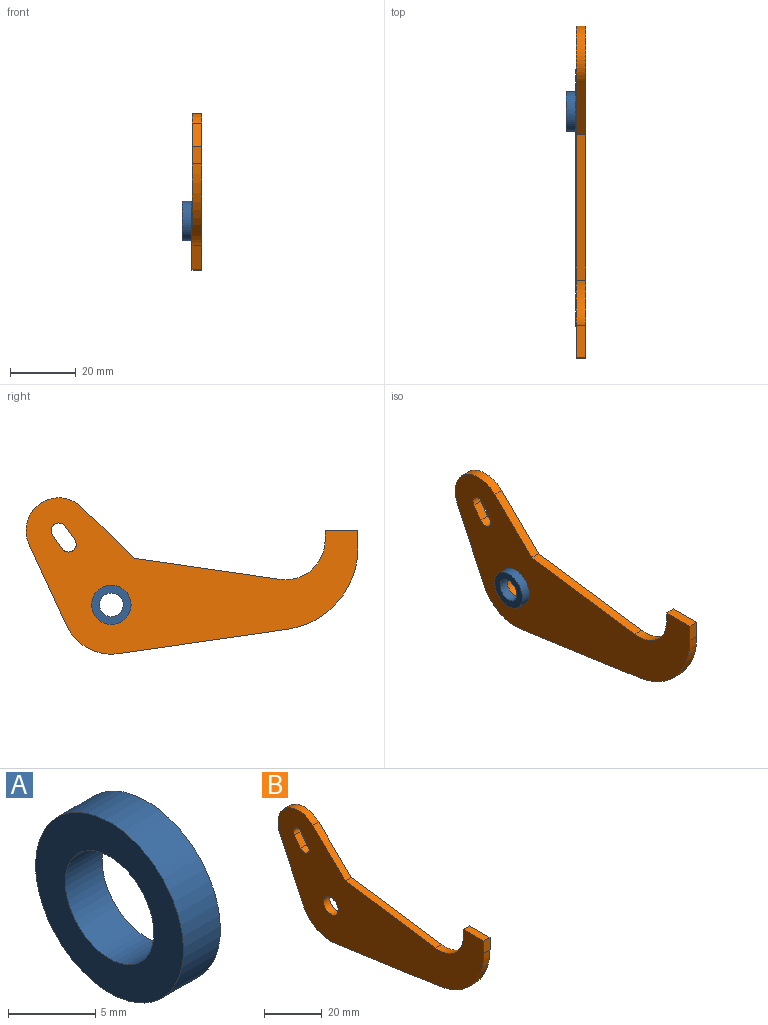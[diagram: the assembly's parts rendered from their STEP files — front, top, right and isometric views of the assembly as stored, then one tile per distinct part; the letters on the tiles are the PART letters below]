
ASSEMBLY  parts=2 mates=1
PART A: 4 faces, bbox 3x12x12 mm
  f0: plane 12x12mm, normal (1,0,0), area 72.4mm2, adj f1,f2
  f1: cylinder r=3.6mm len=7.2mm, axis (-1,0,0), area 67.9mm2, adj f0,f3
  f2: cylinder r=6mm len=12mm, axis (-1,0,0), area 113.1mm2, adj f0,f3
  f3: plane 12x12mm, normal (-1,0,0), area 72.4mm2, adj f1,f2
PART B: 18 faces, bbox 3x101x47.6 mm
  f0: plane 100.95x47.55mm, normal (1,0,0), area 2358.5mm2, adj f1,f2,f3,f4,f5,f6,f7,f8
  f1: cylinder r=2.35mm len=4.27mm, axis (-1,0,0), area 22.1mm2, adj f0,f11,f12,f17
  f2: plane 51.43x7.42mm, normal (0,-0.14,-0.99), area 155.9mm2, adj f0,f3,f10,f17
  f3: cylinder r=15mm len=15.75mm, axis (-1,0,0), area 57.6mm2, adj f0,f2,f4,f17
  f4: plane 24.65x11.41mm, normal (0,0.91,-0.42), area 81.5mm2, adj f0,f3,f5,f17
  f5: cylinder r=10mm len=16.98mm, axis (-1,0,0), area 83.3mm2, adj f0,f4,f6,f17
  f6: plane 15.95x15.56mm, normal (0,-0.7,0.72), area 66.8mm2, adj f0,f5,f7,f17
  f7: plane 44.31x6.4mm, normal (0,-0.14,0.99), area 134.3mm2, adj f0,f6,f8,f17
  f8: cylinder r=12mm len=13.71mm, axis (-1,0,0), area 61.7mm2, adj f0,f7,f9,f17
  f9: plane 3x2.92mm, normal (0,1,0), area 8.8mm2, adj f0,f8,f14,f17
  f10: cylinder r=25mm len=24.74mm, axis (-1,0,0), area 107.1mm2, adj f0,f2,f15,f17
  f11: plane 4.14x3mm, normal (0,-0.82,0.58), area 15.2mm2, adj f0,f1,f13,f17
  f12: plane 4.14x3mm, normal (0,0.82,-0.58), area 15.2mm2, adj f0,f1,f13,f17
  f13: cylinder r=2.35mm len=4.27mm, axis (-1,0,0), area 22.1mm2, adj f0,f11,f12,f17
  f14: plane 10x3mm, normal (0,0,1), area 30mm2, adj f0,f9,f15,f17
  f15: plane 5.23x3mm, normal (0,-1,0), area 15.7mm2, adj f0,f10,f14,f17
  f16: cylinder r=3.6mm len=7.2mm, axis (-1,0,0), area 67.9mm2, adj f0,f17
  f17: plane 100.95x47.55mm, normal (-1,0,0), area 2358.5mm2, adj f1,f2,f3,f4,f5,f6,f7,f8
PLACE A t=(-25,34.16,-14.82)mm
PLACE B t=(-22,34.16,30.28)mm
MATE fastened B.f3 <-> A.f1  axis (-1,0,0) through (-7,10.26,7.73)mm
